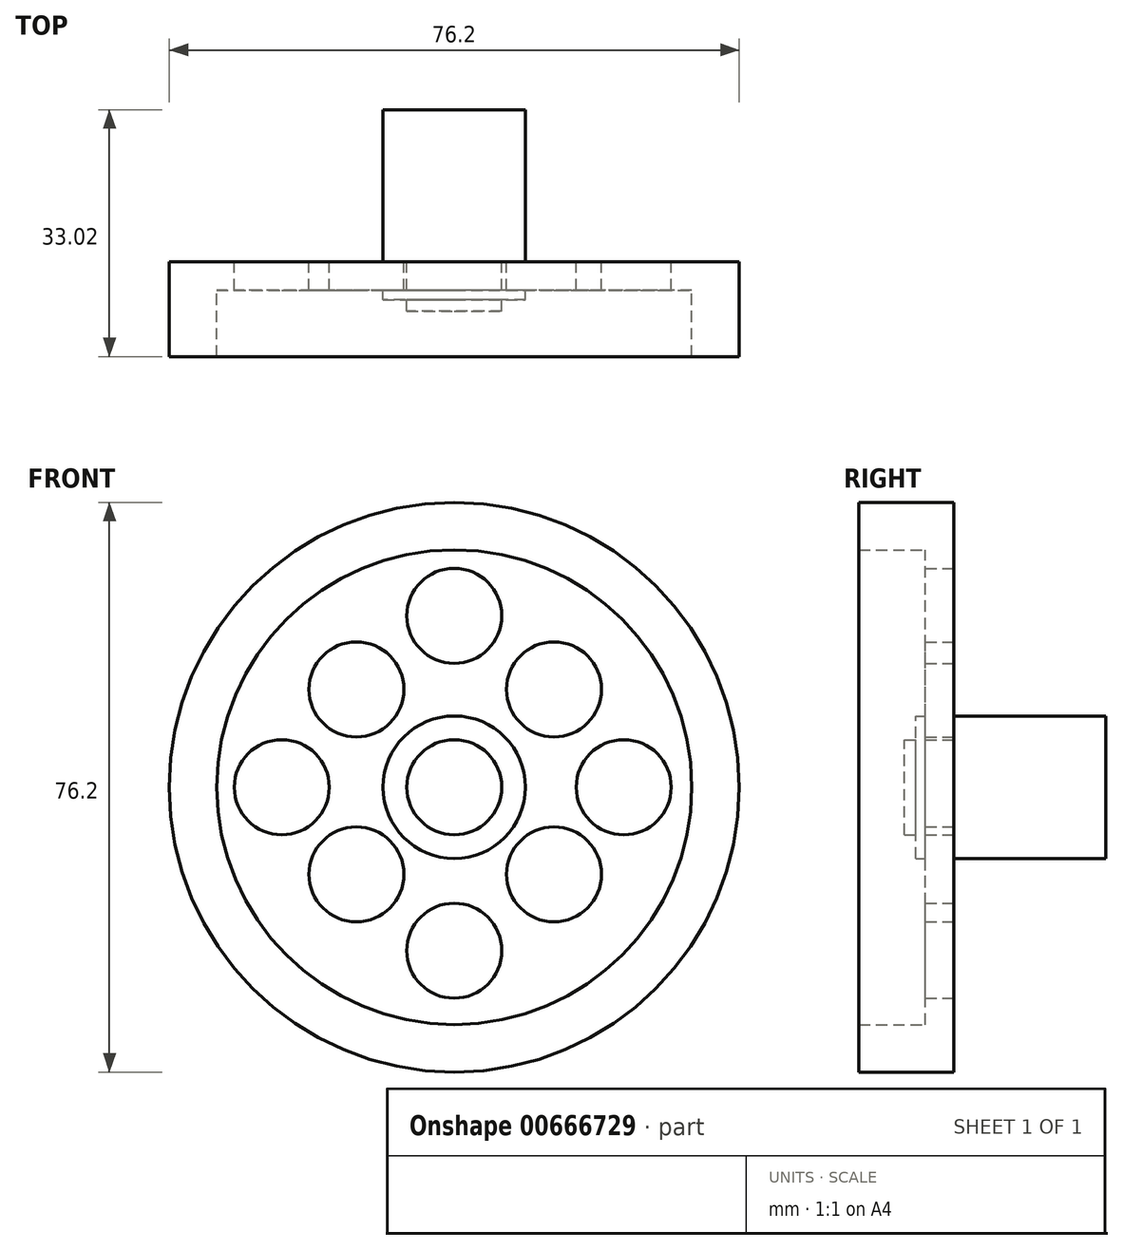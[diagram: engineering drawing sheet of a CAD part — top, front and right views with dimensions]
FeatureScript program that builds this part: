
annotation { "Feature Type Name" : "Feature", "Feature Type Description" : "" }
export const myFeature = defineFeature(function(context is Context, id is Id, definition is map)
    precondition{}
    {
        {
            var Q0;
            Q0=qCreatedBy(makeId("Front.planeOp"),FACE);
            var sketch = newSketch(context, id + "F0", { "sketchPlane" : qUnion([Q0])});
            skCircle(sketch, "E0", {"center": v(0, 0) * mm, "radius": 38.1 * mm});
            skSolve(sketch);
        }
        {
            var Q0;
            Q0=makeQuery(id+"F0.imprint","IMPRINT",FACE,{"disambiguationData":[TD([[makeQuery(id+"F0.imprint","IMPRINT",EDGE,{"derivedFrom":sQuery(id+"F0.wireOp",EDGE,"E0")}),1.0]])]});
            extrude(context, id + "F1", {"entities" : qUnion([Q0]), "depth" : 12.7 * mm, "offsetDistance" : 25.4 * mm});
        }
        {
            var Q0;
            Q0=qCreatedBy(makeId("Front.planeOp"),FACE);
            var sketch = newSketch(context, id + "F2", { "sketchPlane" : qUnion([Q0])});
            skCircle(sketch, "E1", {"center": v(0, 0) * mm, "radius": 31.75 * mm});
            skSolve(sketch);
        }
        {
            var Q0;
            Q0 = qSketchRegion(id + "F2", true);
            extrude(context, id + "F3", {"entities" : qUnion([Q0]), "operationType" : NewBodyOperationType.REMOVE, "depth" : 45.47 * mm, "offsetDistance" : 25.4 * mm});
        }
        {
            var Q0;
            Q0=qCreatedBy(makeId("Front.planeOp"),FACE);
            var sketch = newSketch(context, id + "F4", { "sketchPlane" : qUnion([Q0])});
            skCircle(sketch, "E2", {"center": v(0, 0) * mm, "radius": 34.93 * mm});
            skSolve(sketch);
        }
        {
            var Q0;
            Q0 = qSketchRegion(id + "F4", true);
            extrude(context, id + "F5", {"entities" : qUnion([Q0]), "operationType" : NewBodyOperationType.ADD, "depth" : 3.8 * mm, "offsetDistance" : 25.4 * mm});
        }
        {
            var Q0;
            Q0=qCreatedBy(makeId("Front.planeOp"),FACE);
            var sketch = newSketch(context, id + "F6", { "sketchPlane" : qUnion([Q0])});
            skCircle(sketch, "E3", {"center": v(-13.08, 13.08) * mm, "radius": 6.35 * mm});
            skCircle(sketch, "E4", {"center": v(13.33, 13.08) * mm, "radius": 6.35 * mm});
            skCircle(sketch, "E5", {"center": v(13.33, -11.66) * mm, "radius": 6.35 * mm});
            skCircle(sketch, "E6", {"center": v(-13.08, -11.66) * mm, "radius": 6.35 * mm});
            skSolve(sketch);
        }
        {
            var Q0;
            Q0 = qSketchRegion(id + "F6", true);
            extrude(context, id + "F7", {"entities" : qUnion([Q0]), "operationType" : NewBodyOperationType.REMOVE, "depth" : 38.35 * mm, "offsetDistance" : 25.4 * mm});
        }
        {
            var Q0;
            Q0=qCreatedBy(makeId("Front.planeOp"),FACE);
            var sketch = newSketch(context, id + "F8", { "sketchPlane" : qUnion([Q0])});
            skCircle(sketch, "E7", {"center": v(0, 22.92) * mm, "radius": 6.35 * mm});
            skCircle(sketch, "E8", {"center": v(22.65, 0) * mm, "radius": 6.35 * mm});
            skCircle(sketch, "E9", {"center": v(0, -21.87) * mm, "radius": 6.35 * mm});
            skCircle(sketch, "E10", {"center": v(-23.07, 0) * mm, "radius": 6.35 * mm});
            skSolve(sketch);
        }
        {
            var Q0;
            Q0 = qSketchRegion(id + "F8", true);
            extrude(context, id + "F9", {"entities" : qUnion([Q0]), "operationType" : NewBodyOperationType.REMOVE, "depth" : 26.92 * mm, "offsetDistance" : 25.4 * mm});
        }
        {
            var Q0;
            Q0=qCreatedBy(makeId("Front.planeOp"),FACE);
            var sketch = newSketch(context, id + "F10", { "sketchPlane" : qUnion([Q0])});
            skCircle(sketch, "E11", {"center": v(0, 0) * mm, "radius": 9.53 * mm});
            skSolve(sketch);
        }
        {
            var Q0;
            Q0 = qSketchRegion(id + "F10", true);
            extrude(context, id + "F11", {"entities" : qUnion([Q0]), "operationType" : NewBodyOperationType.ADD, "depth" : 5.08 * mm, "offsetDistance" : 25.4 * mm});
        }
        {
            var Q0;
            Q0=makeQuery(id+"F11.opExtrude","CAP_FACE",FACE,{"disambiguationData":[OSD([sQuery(id+"F10.wireOp",EDGE,"E11")])],"isStart":false});
            extrude(context, id + "F12", {"entities" : qUnion([Q0]), "operationType" : NewBodyOperationType.ADD, "oppositeDirection" : true, "depth" : 25.4 * mm, "offsetDistance" : 25.4 * mm});
        }
        {
            var Q0;
            Q0=qCreatedBy(makeId("Front.planeOp"),FACE);
            var sketch = newSketch(context, id + "F13", { "sketchPlane" : qUnion([Q0])});
            skCircle(sketch, "E12", {"center": v(0, 0) * mm, "radius": 6.35 * mm});
            skSolve(sketch);
        }
        {
            var Q0;
            Q0 = qSketchRegion(id + "F13", true);
            extrude(context, id + "F14", {"entities" : qUnion([Q0]), "operationType" : NewBodyOperationType.ADD, "endBound" : BoundingType.SYMMETRIC, "depth" : 13.2 * mm, "offsetDistance" : 25.4 * mm});
        }
    });
